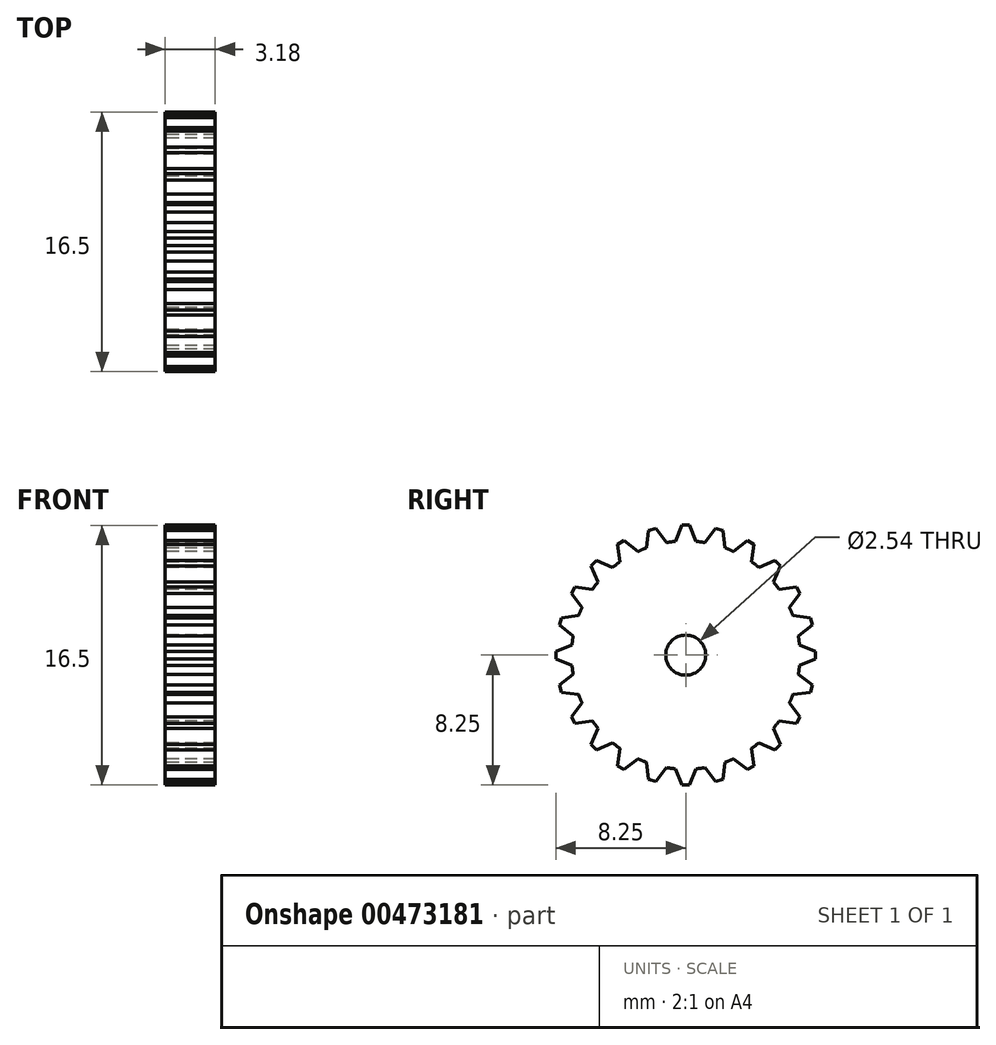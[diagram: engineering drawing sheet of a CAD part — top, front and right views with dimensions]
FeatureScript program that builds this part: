
annotation { "Feature Type Name" : "Feature", "Feature Type Description" : "" }
export const myFeature = defineFeature(function(context is Context, id is Id, definition is map)
    precondition{}
    {
        {
            var Q0;
            Q0=qCreatedBy(makeId("Right.planeOp"),FACE);
            var sketch = newSketch(context, id + "F0", { "sketchPlane" : qUnion([Q0])});
            skCircle(sketch, "E0", {"center": v(0, 0) * mm, "radius": 7.25 * mm});
            skLineSegment(sketch, "E1", {"start": v(-0.66, 7.22) * mm, "end": v(-0.24, 8.25) * mm});
            skLineSegment(sketch, "E2", {"start": v(-0.24, 8.25) * mm, "end": v(0, 8.25) * mm});
            skLineSegment(sketch, "E3.MirrorCS", {"start": v(0.66, 7.22) * mm, "end": v(0.24, 8.25) * mm});
            skLineSegment(sketch, "E4.MirrorCS", {"start": v(0.24, 8.25) * mm, "end": v(0, 8.25) * mm});
            skLineSegment(sketch, "E5.1.1", {"start": v(-1.23, 7.15) * mm, "end": v(-1.9, 8.03) * mm});
            skLineSegment(sketch, "E5.1.2", {"start": v(-1.9, 8.03) * mm, "end": v(-2.14, 7.97) * mm});
            skLineSegment(sketch, "E5.1.3", {"start": v(-2.37, 7.9) * mm, "end": v(-2.14, 7.97) * mm});
            skLineSegment(sketch, "E5.1.4", {"start": v(-2.5, 6.8) * mm, "end": v(-2.37, 7.9) * mm});
            skLineSegment(sketch, "E5.2.1", {"start": v(-3.04, 6.58) * mm, "end": v(-3.92, 7.27) * mm});
            skLineSegment(sketch, "E5.2.2", {"start": v(-3.92, 7.27) * mm, "end": v(-4.13, 7.15) * mm});
            skLineSegment(sketch, "E5.2.3", {"start": v(-4.34, 7.03) * mm, "end": v(-4.13, 7.15) * mm});
            skLineSegment(sketch, "E5.2.4", {"start": v(-4.18, 5.92) * mm, "end": v(-4.34, 7.03) * mm});
            skLineSegment(sketch, "E5.3.1", {"start": v(-4.64, 5.57) * mm, "end": v(-5.66, 6) * mm});
            skLineSegment(sketch, "E5.3.2", {"start": v(-5.66, 6) * mm, "end": v(-5.83, 5.83) * mm});
            skLineSegment(sketch, "E5.3.3", {"start": v(-6, 5.66) * mm, "end": v(-5.83, 5.83) * mm});
            skLineSegment(sketch, "E5.3.4", {"start": v(-5.57, 4.64) * mm, "end": v(-6, 5.66) * mm});
            skLineSegment(sketch, "E5.4.1", {"start": v(-5.92, 4.18) * mm, "end": v(-7.03, 4.34) * mm});
            skLineSegment(sketch, "E5.4.2", {"start": v(-7.03, 4.34) * mm, "end": v(-7.15, 4.13) * mm});
            skLineSegment(sketch, "E5.4.3", {"start": v(-7.27, 3.92) * mm, "end": v(-7.15, 4.13) * mm});
            skLineSegment(sketch, "E5.4.4", {"start": v(-6.58, 3.04) * mm, "end": v(-7.27, 3.92) * mm});
            skLineSegment(sketch, "E5.5.1", {"start": v(-6.8, 2.5) * mm, "end": v(-7.9, 2.37) * mm});
            skLineSegment(sketch, "E5.5.2", {"start": v(-7.9, 2.37) * mm, "end": v(-7.97, 2.14) * mm});
            skLineSegment(sketch, "E5.5.3", {"start": v(-8.03, 1.9) * mm, "end": v(-7.97, 2.14) * mm});
            skLineSegment(sketch, "E5.5.4", {"start": v(-7.15, 1.23) * mm, "end": v(-8.03, 1.9) * mm});
            skLineSegment(sketch, "E5.6.1", {"start": v(-7.22, 0.66) * mm, "end": v(-8.25, 0.24) * mm});
            skLineSegment(sketch, "E5.6.2", {"start": v(-8.25, 0.24) * mm, "end": v(-8.25, 0) * mm});
            skLineSegment(sketch, "E5.6.3", {"start": v(-8.25, -0.24) * mm, "end": v(-8.25, 0) * mm});
            skLineSegment(sketch, "E5.6.4", {"start": v(-7.22, -0.66) * mm, "end": v(-8.25, -0.24) * mm});
            skLineSegment(sketch, "E5.7.1", {"start": v(-7.15, -1.23) * mm, "end": v(-8.03, -1.9) * mm});
            skLineSegment(sketch, "E5.7.2", {"start": v(-8.03, -1.9) * mm, "end": v(-7.97, -2.14) * mm});
            skLineSegment(sketch, "E5.7.3", {"start": v(-7.9, -2.37) * mm, "end": v(-7.97, -2.14) * mm});
            skLineSegment(sketch, "E5.7.4", {"start": v(-6.8, -2.5) * mm, "end": v(-7.9, -2.37) * mm});
            skLineSegment(sketch, "E5.8.1", {"start": v(-6.58, -3.04) * mm, "end": v(-7.27, -3.92) * mm});
            skLineSegment(sketch, "E5.8.2", {"start": v(-7.27, -3.92) * mm, "end": v(-7.15, -4.13) * mm});
            skLineSegment(sketch, "E5.8.3", {"start": v(-7.03, -4.34) * mm, "end": v(-7.15, -4.13) * mm});
            skLineSegment(sketch, "E5.8.4", {"start": v(-5.92, -4.18) * mm, "end": v(-7.03, -4.34) * mm});
            skLineSegment(sketch, "E5.9.1", {"start": v(-5.57, -4.64) * mm, "end": v(-6, -5.66) * mm});
            skLineSegment(sketch, "E5.9.2", {"start": v(-6, -5.66) * mm, "end": v(-5.83, -5.83) * mm});
            skLineSegment(sketch, "E5.9.3", {"start": v(-5.66, -6) * mm, "end": v(-5.83, -5.83) * mm});
            skLineSegment(sketch, "E5.9.4", {"start": v(-4.64, -5.57) * mm, "end": v(-5.66, -6) * mm});
            skLineSegment(sketch, "E5.10.1", {"start": v(-4.18, -5.92) * mm, "end": v(-4.34, -7.03) * mm});
            skLineSegment(sketch, "E5.10.2", {"start": v(-4.34, -7.03) * mm, "end": v(-4.13, -7.15) * mm});
            skLineSegment(sketch, "E5.10.3", {"start": v(-3.92, -7.27) * mm, "end": v(-4.13, -7.15) * mm});
            skLineSegment(sketch, "E5.10.4", {"start": v(-3.04, -6.58) * mm, "end": v(-3.92, -7.27) * mm});
            skLineSegment(sketch, "E5.11.1", {"start": v(-2.5, -6.8) * mm, "end": v(-2.37, -7.9) * mm});
            skLineSegment(sketch, "E5.11.2", {"start": v(-2.37, -7.9) * mm, "end": v(-2.14, -7.97) * mm});
            skLineSegment(sketch, "E5.11.3", {"start": v(-1.9, -8.03) * mm, "end": v(-2.14, -7.97) * mm});
            skLineSegment(sketch, "E5.11.4", {"start": v(-1.23, -7.15) * mm, "end": v(-1.9, -8.03) * mm});
            skLineSegment(sketch, "E5.12.1", {"start": v(-0.66, -7.22) * mm, "end": v(-0.24, -8.25) * mm});
            skLineSegment(sketch, "E5.12.2", {"start": v(-0.24, -8.25) * mm, "end": v(0, -8.25) * mm});
            skLineSegment(sketch, "E5.12.3", {"start": v(0.24, -8.25) * mm, "end": v(0, -8.25) * mm});
            skLineSegment(sketch, "E5.12.4", {"start": v(0.66, -7.22) * mm, "end": v(0.24, -8.25) * mm});
            skLineSegment(sketch, "E5.13.1", {"start": v(1.23, -7.15) * mm, "end": v(1.9, -8.03) * mm});
            skLineSegment(sketch, "E5.13.2", {"start": v(1.9, -8.03) * mm, "end": v(2.14, -7.97) * mm});
            skLineSegment(sketch, "E5.13.3", {"start": v(2.37, -7.9) * mm, "end": v(2.14, -7.97) * mm});
            skLineSegment(sketch, "E5.13.4", {"start": v(2.5, -6.8) * mm, "end": v(2.37, -7.9) * mm});
            skLineSegment(sketch, "E5.14.1", {"start": v(3.04, -6.58) * mm, "end": v(3.92, -7.27) * mm});
            skLineSegment(sketch, "E5.14.2", {"start": v(3.92, -7.27) * mm, "end": v(4.13, -7.15) * mm});
            skLineSegment(sketch, "E5.14.3", {"start": v(4.34, -7.03) * mm, "end": v(4.13, -7.15) * mm});
            skLineSegment(sketch, "E5.14.4", {"start": v(4.18, -5.92) * mm, "end": v(4.34, -7.03) * mm});
            skLineSegment(sketch, "E5.15.1", {"start": v(4.64, -5.57) * mm, "end": v(5.66, -6) * mm});
            skLineSegment(sketch, "E5.15.2", {"start": v(5.66, -6) * mm, "end": v(5.83, -5.83) * mm});
            skLineSegment(sketch, "E5.15.3", {"start": v(6, -5.66) * mm, "end": v(5.83, -5.83) * mm});
            skLineSegment(sketch, "E5.15.4", {"start": v(5.57, -4.64) * mm, "end": v(6, -5.66) * mm});
            skLineSegment(sketch, "E5.16.1", {"start": v(5.92, -4.18) * mm, "end": v(7.03, -4.34) * mm});
            skLineSegment(sketch, "E5.16.2", {"start": v(7.03, -4.34) * mm, "end": v(7.15, -4.13) * mm});
            skLineSegment(sketch, "E5.16.3", {"start": v(7.27, -3.92) * mm, "end": v(7.15, -4.13) * mm});
            skLineSegment(sketch, "E5.16.4", {"start": v(6.58, -3.04) * mm, "end": v(7.27, -3.92) * mm});
            skLineSegment(sketch, "E5.17.1", {"start": v(6.8, -2.5) * mm, "end": v(7.9, -2.37) * mm});
            skLineSegment(sketch, "E5.17.2", {"start": v(7.9, -2.37) * mm, "end": v(7.97, -2.14) * mm});
            skLineSegment(sketch, "E5.17.3", {"start": v(8.03, -1.9) * mm, "end": v(7.97, -2.14) * mm});
            skLineSegment(sketch, "E5.17.4", {"start": v(7.15, -1.23) * mm, "end": v(8.03, -1.9) * mm});
            skLineSegment(sketch, "E5.18.1", {"start": v(7.22, -0.66) * mm, "end": v(8.25, -0.24) * mm});
            skLineSegment(sketch, "E5.18.2", {"start": v(8.25, -0.24) * mm, "end": v(8.25, 0) * mm});
            skLineSegment(sketch, "E5.18.3", {"start": v(8.25, 0.24) * mm, "end": v(8.25, 0) * mm});
            skLineSegment(sketch, "E5.18.4", {"start": v(7.22, 0.66) * mm, "end": v(8.25, 0.24) * mm});
            skLineSegment(sketch, "E5.19.1", {"start": v(7.15, 1.23) * mm, "end": v(8.03, 1.9) * mm});
            skLineSegment(sketch, "E5.19.2", {"start": v(8.03, 1.9) * mm, "end": v(7.97, 2.14) * mm});
            skLineSegment(sketch, "E5.19.3", {"start": v(7.9, 2.37) * mm, "end": v(7.97, 2.14) * mm});
            skLineSegment(sketch, "E5.19.4", {"start": v(6.8, 2.5) * mm, "end": v(7.9, 2.37) * mm});
            skLineSegment(sketch, "E5.20.1", {"start": v(6.58, 3.04) * mm, "end": v(7.27, 3.92) * mm});
            skLineSegment(sketch, "E5.20.2", {"start": v(7.27, 3.92) * mm, "end": v(7.15, 4.13) * mm});
            skLineSegment(sketch, "E5.20.3", {"start": v(7.03, 4.34) * mm, "end": v(7.15, 4.13) * mm});
            skLineSegment(sketch, "E5.20.4", {"start": v(5.92, 4.18) * mm, "end": v(7.03, 4.34) * mm});
            skLineSegment(sketch, "E5.21.1", {"start": v(5.57, 4.64) * mm, "end": v(6, 5.66) * mm});
            skLineSegment(sketch, "E5.21.2", {"start": v(6, 5.66) * mm, "end": v(5.83, 5.83) * mm});
            skLineSegment(sketch, "E5.21.3", {"start": v(5.66, 6) * mm, "end": v(5.83, 5.83) * mm});
            skLineSegment(sketch, "E5.21.4", {"start": v(4.64, 5.57) * mm, "end": v(5.66, 6) * mm});
            skLineSegment(sketch, "E5.22.1", {"start": v(4.18, 5.92) * mm, "end": v(4.34, 7.03) * mm});
            skLineSegment(sketch, "E5.22.2", {"start": v(4.34, 7.03) * mm, "end": v(4.13, 7.15) * mm});
            skLineSegment(sketch, "E5.22.3", {"start": v(3.92, 7.27) * mm, "end": v(4.13, 7.15) * mm});
            skLineSegment(sketch, "E5.22.4", {"start": v(3.04, 6.58) * mm, "end": v(3.92, 7.27) * mm});
            skLineSegment(sketch, "E5.23.1", {"start": v(2.5, 6.8) * mm, "end": v(2.37, 7.9) * mm});
            skLineSegment(sketch, "E5.23.2", {"start": v(2.37, 7.9) * mm, "end": v(2.14, 7.97) * mm});
            skLineSegment(sketch, "E5.23.3", {"start": v(1.9, 8.03) * mm, "end": v(2.14, 7.97) * mm});
            skLineSegment(sketch, "E5.23.4", {"start": v(1.23, 7.15) * mm, "end": v(1.9, 8.03) * mm});
            skCircle(sketch, "E6", {"center": v(0, 0) * mm, "radius": 1.27 * mm});
            skSolve(sketch);
        }
        {
            var Q0;
            {var subQ1=sQuery(id+"F0.wireOp",EDGE,"E1");Q0=makeQuery(id+"F0.imprint","IMPRINT",FACE,{"disambiguationData":[TD([[makeQuery(id+"F0.imprint","IMPRINT",EDGE,{"derivedFrom":subQ1}),-1.0]])]});}
            var Q1;
            Q1=makeQuery(id+"F0.imprint","IMPRINT",FACE,{"disambiguationData":[TD([[makeQuery(id+"F0.imprint","IMPRINT",EDGE,{"derivedFrom":sQuery(id+"F0.wireOp",EDGE,"E6")}),-1.0]])]});
            var Q2;
            {var subQ0=sQuery(id+"F0.wireOp",EDGE,"E5.23.1");Q2=makeQuery(id+"F0.imprint","IMPRINT",FACE,{"disambiguationData":[TD([[makeQuery(id+"F0.imprint","IMPRINT",EDGE,{"derivedFrom":subQ0}),1.0]])]});}
            var Q3;
            {var subQ1=sQuery(id+"F0.wireOp",EDGE,"E5.22.1");Q3=makeQuery(id+"F0.imprint","IMPRINT",FACE,{"disambiguationData":[TD([[makeQuery(id+"F0.imprint","IMPRINT",EDGE,{"derivedFrom":subQ1}),1.0]])]});}
            var Q4;
            {var subQ1=sQuery(id+"F0.wireOp",EDGE,"E5.21.1");Q4=makeQuery(id+"F0.imprint","IMPRINT",FACE,{"disambiguationData":[TD([[makeQuery(id+"F0.imprint","IMPRINT",EDGE,{"derivedFrom":subQ1}),1.0]])]});}
            var Q5;
            {var subQ1=sQuery(id+"F0.wireOp",EDGE,"E5.20.1");Q5=makeQuery(id+"F0.imprint","IMPRINT",FACE,{"disambiguationData":[TD([[makeQuery(id+"F0.imprint","IMPRINT",EDGE,{"derivedFrom":subQ1}),1.0]])]});}
            var Q6;
            {var subQ2=sQuery(id+"F0.wireOp",EDGE,"E5.19.1");Q6=makeQuery(id+"F0.imprint","IMPRINT",FACE,{"disambiguationData":[TD([[makeQuery(id+"F0.imprint","IMPRINT",EDGE,{"derivedFrom":subQ2}),1.0]])]});}
            var Q7;
            {var subQ1=sQuery(id+"F0.wireOp",EDGE,"E5.18.1");Q7=makeQuery(id+"F0.imprint","IMPRINT",FACE,{"disambiguationData":[TD([[makeQuery(id+"F0.imprint","IMPRINT",EDGE,{"derivedFrom":subQ1}),1.0]])]});}
            var Q8;
            {var subQ1=sQuery(id+"F0.wireOp",EDGE,"E5.17.1");Q8=makeQuery(id+"F0.imprint","IMPRINT",FACE,{"disambiguationData":[TD([[makeQuery(id+"F0.imprint","IMPRINT",EDGE,{"derivedFrom":subQ1}),1.0]])]});}
            var Q9;
            {var subQ1=sQuery(id+"F0.wireOp",EDGE,"E5.16.1");Q9=makeQuery(id+"F0.imprint","IMPRINT",FACE,{"disambiguationData":[TD([[makeQuery(id+"F0.imprint","IMPRINT",EDGE,{"derivedFrom":subQ1}),1.0]])]});}
            var Q10;
            {var subQ1=sQuery(id+"F0.wireOp",EDGE,"E5.15.1");Q10=makeQuery(id+"F0.imprint","IMPRINT",FACE,{"disambiguationData":[TD([[makeQuery(id+"F0.imprint","IMPRINT",EDGE,{"derivedFrom":subQ1}),1.0]])]});}
            var Q11;
            {var subQ2=sQuery(id+"F0.wireOp",EDGE,"E5.14.1");Q11=makeQuery(id+"F0.imprint","IMPRINT",FACE,{"disambiguationData":[TD([[makeQuery(id+"F0.imprint","IMPRINT",EDGE,{"derivedFrom":subQ2}),1.0]])]});}
            var Q12;
            {var subQ2=sQuery(id+"F0.wireOp",EDGE,"E5.13.1");Q12=makeQuery(id+"F0.imprint","IMPRINT",FACE,{"disambiguationData":[TD([[makeQuery(id+"F0.imprint","IMPRINT",EDGE,{"derivedFrom":subQ2}),1.0]])]});}
            var Q13;
            {var subQ1=sQuery(id+"F0.wireOp",EDGE,"E5.12.1");Q13=makeQuery(id+"F0.imprint","IMPRINT",FACE,{"disambiguationData":[TD([[makeQuery(id+"F0.imprint","IMPRINT",EDGE,{"derivedFrom":subQ1}),1.0]])]});}
            var Q14;
            {var subQ1=sQuery(id+"F0.wireOp",EDGE,"E5.11.1");Q14=makeQuery(id+"F0.imprint","IMPRINT",FACE,{"disambiguationData":[TD([[makeQuery(id+"F0.imprint","IMPRINT",EDGE,{"derivedFrom":subQ1}),1.0]])]});}
            var Q15;
            {var subQ1=sQuery(id+"F0.wireOp",EDGE,"E5.10.1");Q15=makeQuery(id+"F0.imprint","IMPRINT",FACE,{"disambiguationData":[TD([[makeQuery(id+"F0.imprint","IMPRINT",EDGE,{"derivedFrom":subQ1}),1.0]])]});}
            var Q16;
            {var subQ1=sQuery(id+"F0.wireOp",EDGE,"E5.9.1");Q16=makeQuery(id+"F0.imprint","IMPRINT",FACE,{"disambiguationData":[TD([[makeQuery(id+"F0.imprint","IMPRINT",EDGE,{"derivedFrom":subQ1}),1.0]])]});}
            var Q17;
            {var subQ1=sQuery(id+"F0.wireOp",EDGE,"E5.8.1");Q17=makeQuery(id+"F0.imprint","IMPRINT",FACE,{"disambiguationData":[TD([[makeQuery(id+"F0.imprint","IMPRINT",EDGE,{"derivedFrom":subQ1}),1.0]])]});}
            var Q18;
            {var subQ1=sQuery(id+"F0.wireOp",EDGE,"E5.6.1");Q18=makeQuery(id+"F0.imprint","IMPRINT",FACE,{"disambiguationData":[TD([[makeQuery(id+"F0.imprint","IMPRINT",EDGE,{"derivedFrom":subQ1}),1.0]])]});}
            var Q19;
            {var subQ2=sQuery(id+"F0.wireOp",EDGE,"E5.5.1");Q19=makeQuery(id+"F0.imprint","IMPRINT",FACE,{"disambiguationData":[TD([[makeQuery(id+"F0.imprint","IMPRINT",EDGE,{"derivedFrom":subQ2}),1.0]])]});}
            var Q20;
            {var subQ2=sQuery(id+"F0.wireOp",EDGE,"E5.4.1");Q20=makeQuery(id+"F0.imprint","IMPRINT",FACE,{"disambiguationData":[TD([[makeQuery(id+"F0.imprint","IMPRINT",EDGE,{"derivedFrom":subQ2}),1.0]])]});}
            var Q21;
            {var subQ1=sQuery(id+"F0.wireOp",EDGE,"E5.3.1");Q21=makeQuery(id+"F0.imprint","IMPRINT",FACE,{"disambiguationData":[TD([[makeQuery(id+"F0.imprint","IMPRINT",EDGE,{"derivedFrom":subQ1}),1.0]])]});}
            var Q22;
            {var subQ1=sQuery(id+"F0.wireOp",EDGE,"E5.2.1");Q22=makeQuery(id+"F0.imprint","IMPRINT",FACE,{"disambiguationData":[TD([[makeQuery(id+"F0.imprint","IMPRINT",EDGE,{"derivedFrom":subQ1}),1.0]])]});}
            var Q23;
            {var subQ1=sQuery(id+"F0.wireOp",EDGE,"E5.1.1");Q23=makeQuery(id+"F0.imprint","IMPRINT",FACE,{"disambiguationData":[TD([[makeQuery(id+"F0.imprint","IMPRINT",EDGE,{"derivedFrom":subQ1}),1.0]])]});}
            var Q24;
            {var subQ1=sQuery(id+"F0.wireOp",EDGE,"E5.7.1");Q24=makeQuery(id+"F0.imprint","IMPRINT",FACE,{"disambiguationData":[TD([[makeQuery(id+"F0.imprint","IMPRINT",EDGE,{"derivedFrom":subQ1}),1.0]])]});}
            extrude(context, id + "F1", {"entities" : qUnion([Q0, Q1, Q2, Q3, Q4, Q5, Q6, Q7, Q8, Q9, Q10, Q11, Q12, Q13, Q14, Q15, Q16, Q17, Q18, Q19, Q20, Q21, Q22, Q23, Q24]), "depth" : 3.17 * mm});
        }
    });
